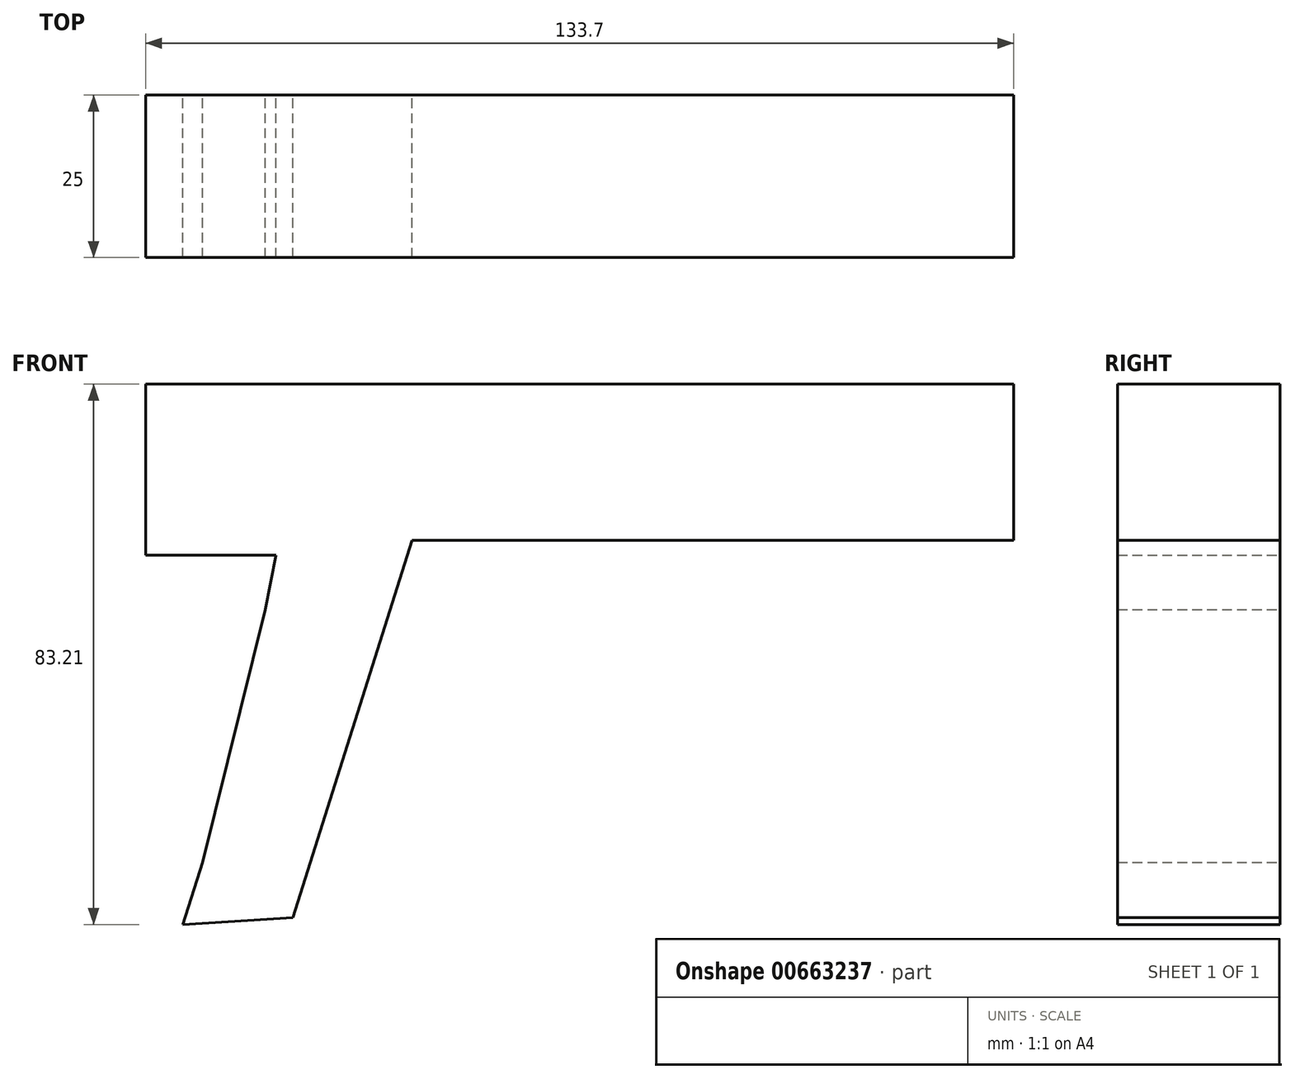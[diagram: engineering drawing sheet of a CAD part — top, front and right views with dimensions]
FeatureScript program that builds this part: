
annotation { "Feature Type Name" : "Feature", "Feature Type Description" : "" }
export const myFeature = defineFeature(function(context is Context, id is Id, definition is map)
    precondition{}
    {
        {
            var Q0;
            Q0=qCreatedBy(makeId("Front.planeOp"),FACE);
            var sketch = newSketch(context, id + "F0", { "sketchPlane" : qUnion([Q0])});
            skLineSegment(sketch, "E0", {"start": v(-66.43, 0) * mm, "end": v(-76.06, -38.95) * mm});
            skLineSegment(sketch, "E1", {"start": v(-62.18, -47.45) * mm, "end": v(-43.77, 10.62) * mm});
            skLineSegment(sketch, "E2", {"start": v(-43.77, 10.62) * mm, "end": v(48.86, 10.62) * mm});
            skLineSegment(sketch, "E3", {"start": v(48.86, 10.62) * mm, "end": v(48.86, 34.7) * mm});
            skLineSegment(sketch, "E4", {"start": v(48.86, 34.7) * mm, "end": v(-84.84, 34.7) * mm});
            skLineSegment(sketch, "E5", {"start": v(-84.84, 34.7) * mm, "end": v(-84.84, 8.36) * mm});
            skLineSegment(sketch, "E6", {"start": v(-84.84, 8.36) * mm, "end": v(-64.73, 8.36) * mm});
            skLineSegment(sketch, "E7", {"start": v(-64.73, 8.36) * mm, "end": v(-66.43, 0) * mm});
            skLineSegment(sketch, "E8", {"start": v(-76.06, -38.95) * mm, "end": v(-79.09, -48.5) * mm});
            skLineSegment(sketch, "E9", {"start": v(-79.09, -48.5) * mm, "end": v(-62.18, -47.45) * mm});
            skSolve(sketch);
        }
        {
            var Q0;
            Q0=makeQuery(id+"F0.imprint","IMPRINT",FACE,{"disambiguationData":[TD([[makeQuery(id+"F0.imprint","IMPRINT",EDGE,{"derivedFrom":sQuery(id+"F0.wireOp",EDGE,"E0")}),1.0]])]});
            extrude(context, id + "F1", {"entities" : qUnion([Q0]), "depth" : 25 * mm, "offsetDistance" : 25 * mm});
        }
        {
            var Q0;
            Q0=qCreatedBy(makeId("Right.planeOp"),FACE);
            var sketch = newSketch(context, id + "F2", { "sketchPlane" : qUnion([Q0])});
            skCircle(sketch, "E10", {"center": v(-12.04, 23.37) * mm, "radius": 9.25 * mm});
            skSolve(sketch);
        }
        {
            var Q0;
            Q0=sQuery(id+"F2.wireOp",EDGE,"E10");
            extrude(context, id + "F3", {"bodyType" : ToolBodyType.SURFACE, "surfaceEntities" : qUnion([Q0]), "depth" : 66.4 * mm, "offsetDistance" : 25 * mm});
        }
    });
